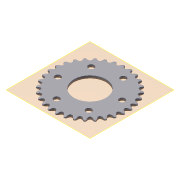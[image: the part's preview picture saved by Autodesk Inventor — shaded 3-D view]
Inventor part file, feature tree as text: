
AUTODESK INVENTOR PART (.ipt)
format: ipt  version: 2011 (Build 150239000, 239)  size: 811,520 bytes
history: native  units: mm
features: other x6, extrude x2, hole x2, sketch x2, pattern_linear x1, pattern_circular x1, plane x1
ambient origin geometry x8: Origin, YZ Plane, XZ Plane, XY Plane, X Axis, Y Axis, Z Axis, Center Point
bodies: Solid1 (feature_tree)
feature tree (15):
  other  "Theoretical Tooth Profile"
  other  "Tooth Profile"
  other  "Section Profile"
  other  "Shroud"
  other  "Strand"
  pattern_linear  "Strand Pattern"  Spacing1=1.697355mm  [1 undecoded]
  extrude  "Theoretical Tooth"  Depth=22.143865mm
  extrude  "Tooth"  Depth=2.83616mm
  pattern_circular  "Tooth Pattern"  [2 undecoded]
  other  "Timing Plane"
  hole  "Hole1"  [1 undecoded]
  hole  "Hole2"  [1 undecoded]
  plane  "Work Plane3"
  sketch  "Sketch4"  dims[d0=64.784587mm]
  sketch  "Sketch5"  dims[d2=1.963495mm d3=1.697355mm d10=22.143865mm d11=2.83616mm d12=2.6416mm d13=4.338955mm d14=4.6228mm d18=10.0mm d19=0.0mm d20=320.0mm d21=360.0deg d23=1.905mm d28=0.0mm d29=0.0mm d30=2.286mm d31=56.852632mm d32=2.286mm d33=0.79375mm d34=6.75005mm d36=90.0deg d37=90.0deg d38=10.0mm d40=6.4008mm d42=0.0mm d43=1.143mm d44=23.943736mm d45=1.697355mm d46=13.47216mm d47=0.0mm d48=25.4mm d49=0.0mm d50=10.0mm d51=28.5623mm d52=19.05mm d53=9.525mm d54=6.35mm d55=14.3117mm d56=25.4mm d57=20.594885mm d58=47.625mm d59=60.0mm d61=360.0deg d63=5.2324mm d64=19.05mm d65=9.525mm d66=6.35mm d67=14.3117mm d68=25.4mm d69=20.594885mm d70=0.0mm]
note: 5 required parameter values undecoded (feature->parameter linkage not recoverable at this tier; creation-order binding heuristic only, values carry confidence <= 0.55)
